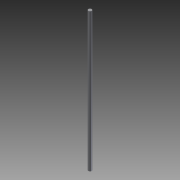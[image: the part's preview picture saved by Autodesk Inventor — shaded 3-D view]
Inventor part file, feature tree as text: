
AUTODESK INVENTOR PART (.ipt)
format: ipt  version: 2012 (Build 160160000, 160)  size: 60,928 bytes
history: native  units: mm
features: extrude x1, sketch x1
ambient origin geometry x8: Origin, YZ Plane, XZ Plane, XY Plane, X Axis, Y Axis, Z Axis, Center Point
bodies: Solid1 (feature_tree)
feature tree (2):
  extrude  "Extrusion1"  Depth=330.0mm TaperAngle=0.0deg
  sketch  "Sketch1"  dims[d0=8.0mm d1=330.0mm d2=0.0mm]
